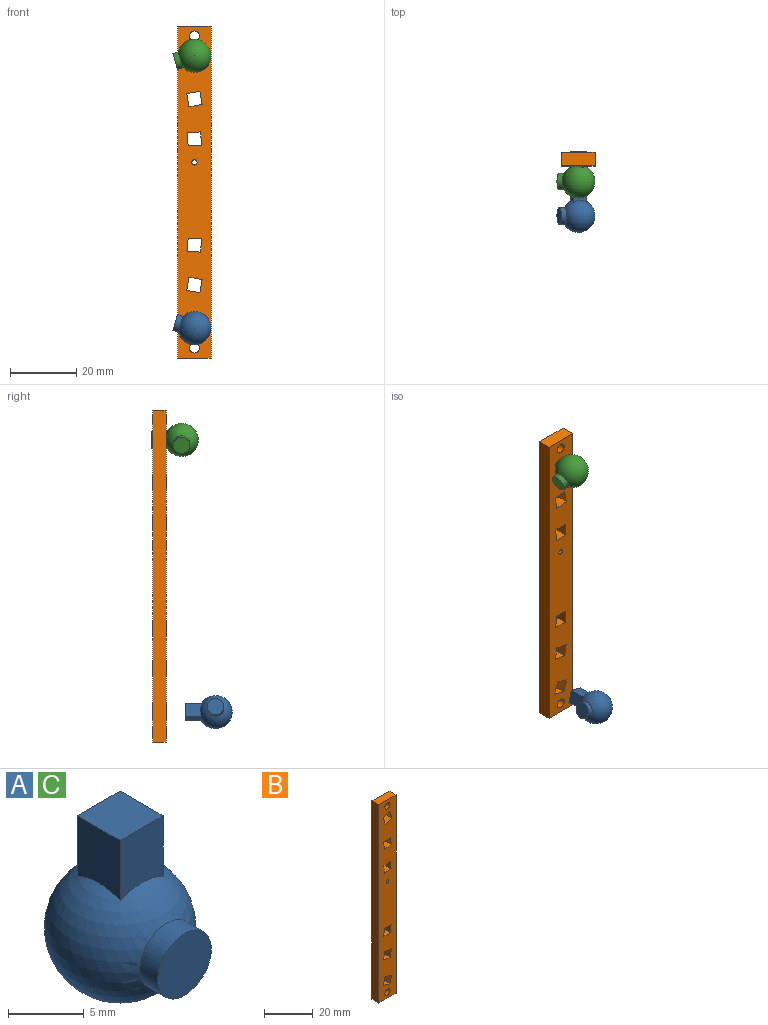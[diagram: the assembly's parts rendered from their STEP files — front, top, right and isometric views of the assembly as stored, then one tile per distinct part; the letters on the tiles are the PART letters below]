
ASSEMBLY  parts=3 mates=4
PART A: 8 faces, bbox 10x11x14 mm
  f0: cylinder r=2.5mm len=5mm, axis (0,1,0), area 26.2mm2, adj f1,f2
  f1: plane 5x5mm, normal (0,-1,0), area 19.6mm2, adj f0
  f2: sphere r=5mm, area 276.1mm2, adj f0,f3,f4,f5,f6
  f3: plane 4.88x4mm, normal (1,0,0), area 18.3mm2, adj f2,f4,f6,f7
  f4: plane 4.88x4mm, normal (0,1,0), area 18.3mm2, adj f2,f3,f5,f7
  f5: plane 4.88x4mm, normal (-1,0,0), area 18.3mm2, adj f2,f4,f6,f7
  f6: plane 4.88x4mm, normal (0,-1,0), area 18.3mm2, adj f2,f3,f5,f7
  f7: plane 4x4mm, normal (0,0,1), area 16mm2, adj f3,f4,f5,f6
PART B: 33 faces, bbox 10x4x100 mm
  f0: plane 100x10mm, normal (0,-1,0), area 887.9mm2, adj f2,f3,f4,f5,f6,f7,f8,f9
  f1: plane 100x10mm, normal (0,1,0), area 887.9mm2, adj f2,f3,f4,f5,f6,f7,f8,f9
  f2: plane 100x4mm, normal (1,0,0), area 400mm2, adj f0,f1,f3,f5
  f3: plane 10x4mm, normal (0,0,1), area 40mm2, adj f0,f1,f2,f4
  f4: plane 100x4mm, normal (-1,0,0), area 400mm2, adj f0,f1,f3,f5
  f5: plane 10x4mm, normal (0,0,-1), area 40mm2, adj f0,f1,f2,f4
  f6: plane 4x4mm, normal (-1,0,-0.05), area 16mm2, adj f0,f1,f7,f9
  f7: plane 4x4mm, normal (0.05,0,-1), area 16mm2, adj f0,f1,f6,f8
  f8: plane 4x4mm, normal (1,0,0.05), area 16mm2, adj f0,f1,f7,f9
  f9: plane 4x4mm, normal (-0.05,0,1), area 16mm2, adj f0,f1,f6,f8
  f10: plane 4x3.94mm, normal (-0.99,0,-0.17), area 16mm2, adj f0,f1,f11,f13
  f11: plane 4x3.94mm, normal (0.17,0,-0.99), area 16mm2, adj f0,f1,f10,f12
  f12: plane 4x3.94mm, normal (0.99,0,0.17), area 16mm2, adj f0,f1,f11,f13
  f13: plane 4x3.94mm, normal (-0.17,0,0.99), area 16mm2, adj f0,f1,f10,f12
  f14: plane 4x3.85mm, normal (-0.96,0,-0.28), area 16mm2, adj f0,f1,f15,f17
  f15: plane 4x3.85mm, normal (0.28,0,-0.96), area 16mm2, adj f0,f1,f14,f16
  f16: plane 4x3.85mm, normal (0.96,0,0.28), area 16mm2, adj f0,f1,f15,f17
  f17: plane 4x3.85mm, normal (-0.28,0,0.96), area 16mm2, adj f0,f1,f14,f16
  f18: cylinder r=1.5mm len=4mm, axis (0,1,0), area 37.7mm2, adj f0,f1
  f19: plane 4x4mm, normal (-1,0,0.05), area 16mm2, adj f0,f1,f20,f22
  f20: plane 4x4mm, normal (-0.05,0,-1), area 16mm2, adj f0,f1,f19,f21
  f21: plane 4x4mm, normal (1,0,-0.05), area 16mm2, adj f0,f1,f20,f22
  f22: plane 4x4mm, normal (0.05,0,1), area 16mm2, adj f0,f1,f19,f21
  f23: plane 4x3.94mm, normal (-0.99,0,0.17), area 16mm2, adj f0,f1,f24,f26
  f24: plane 4x3.94mm, normal (-0.17,0,-0.99), area 16mm2, adj f0,f1,f23,f25
  f25: plane 4x3.94mm, normal (0.99,0,-0.17), area 16mm2, adj f0,f1,f24,f26
  f26: plane 4x3.94mm, normal (0.17,0,0.99), area 16mm2, adj f0,f1,f23,f25
  f27: plane 4x3.85mm, normal (-0.96,0,0.28), area 16mm2, adj f0,f1,f28,f30
  f28: plane 4x3.85mm, normal (-0.28,0,-0.96), area 16mm2, adj f0,f1,f27,f29
  f29: plane 4x3.85mm, normal (0.96,0,-0.28), area 16mm2, adj f0,f1,f28,f30
  f30: plane 4x3.85mm, normal (0.28,0,0.96), area 16mm2, adj f0,f1,f27,f29
  f31: cylinder r=1.5mm len=4mm, axis (0,1,0), area 37.7mm2, adj f0,f1
  f32: cylinder r=0.8mm len=4mm, axis (0,1,0), area 20.1mm2, adj f0,f1
PART C: same geometry as A
PLACE A rot(axis=(-0.68,-0.52,-0.52),111.2deg) t=(0.55,-17.06,-33.93)mm
PLACE B t=(0.55,-0.14,7.07)mm
PLACE C rot(axis=(-0.47,-0.62,-0.62),129.6deg) t=(0.55,-6.85,48.07)mm
MATE planar A.f6 <-> B.f29  axis (-0.96,0,0.28) through (-1.37,-10.35,-33.38)mm
MATE planar A.f3 <-> B.f28  axis (0.28,0,0.96) through (1.11,-10.35,-32.01)mm
MATE planar C.f6 <-> B.f16  axis (-0.96,0,-0.28) through (-1.37,-0.14,47.52)mm
MATE planar C.f3 <-> B.f15  axis (-0.28,0,0.96) through (0,-0.14,49.99)mm
